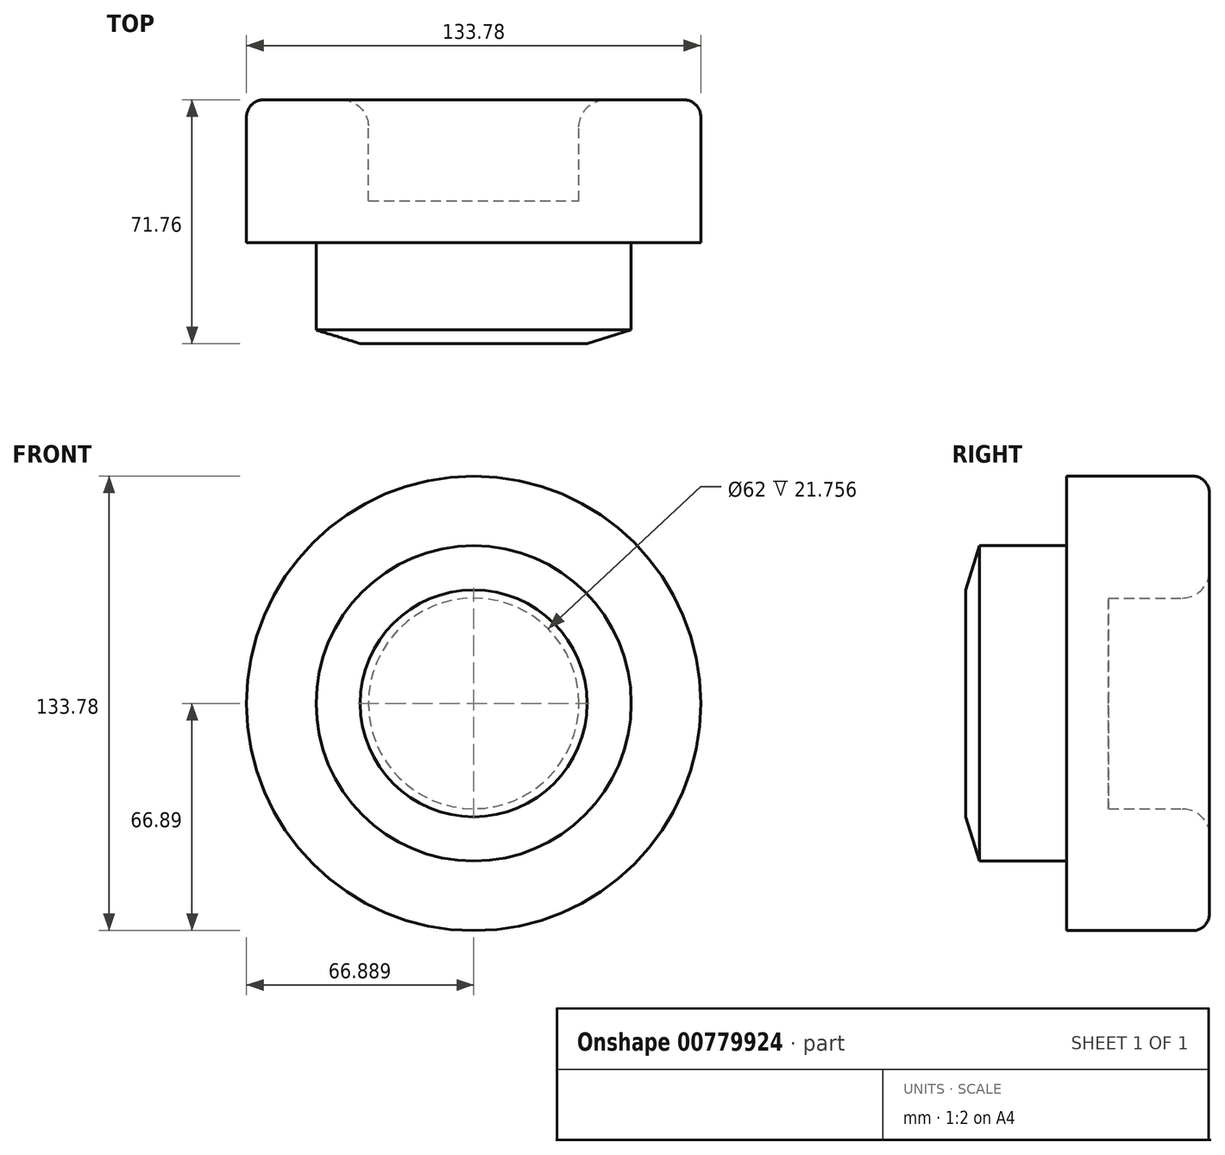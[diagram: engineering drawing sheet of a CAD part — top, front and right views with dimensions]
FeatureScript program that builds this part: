
annotation { "Feature Type Name" : "Feature", "Feature Type Description" : "" }
export const myFeature = defineFeature(function(context is Context, id is Id, definition is map)
    precondition{}
    {
        {
            var Q0;
            Q0=qCreatedBy(makeId("Top.planeOp"),FACE);
            var sketch = newSketch(context, id + "F0", { "sketchPlane" : qUnion([Q0])});
            skLineSegment(sketch, "E0.top", {"start": v(-14.36, -20) * mm, "end": v(32.04, -20) * mm});
            skLineSegment(sketch, "E0.left", {"start": v(-14.36, 22) * mm, "end": v(-14.36, -20) * mm});
            skLineSegment(sketch, "E0.right", {"start": v(32.04, 9.67) * mm, "end": v(32.04, -20) * mm});
            skLineSegment(sketch, "E1.bottom", {"start": v(16.64, 51.76) * mm, "end": v(47.53, 51.76) * mm});
            skLineSegment(sketch, "E1.top", {"start": v(32.04, 9.67) * mm, "end": v(52.53, 9.67) * mm});
            skLineSegment(sketch, "E1.right", {"start": v(52.53, 46.76) * mm, "end": v(52.53, 9.67) * mm});
            skPoint(sketch, "E2.visualSharp", {"position": v(52.53, 51.76) * mm});
            skArc(sketch, "E2.filletArc", {"start": v(52.53, 46.76) * mm, "mid": v(51.07, 50.3) * mm, "end": v(47.53, 51.76) * mm});
            skLineSegment(sketch, "E3.0", {"start": v(-14.36, 22) * mm, "end": v(16.64, 22) * mm});
            skLineSegment(sketch, "E3.1", {"start": v(16.64, 51.76) * mm, "end": v(16.64, 22) * mm});
            skSolve(sketch);
        }
        {
            var Q0;
            Q0=makeQuery(id+"F0.imprint","IMPRINT",FACE,{"disambiguationData":[TD([[makeQuery(id+"F0.imprint","IMPRINT",EDGE,{"derivedFrom":sQuery(id+"F0.wireOp",EDGE,"E0.top")}),1.0]])]});
            var Q1;
            Q1=sQuery(id+"F0.wireOp",EDGE,"E0.left");
            revolve(context, id + "F1", {"surfaceOperationType" : NewSurfaceOperationType.NEW, "entities" : qUnion([Q0]), "axis" : qUnion([Q1]), "revolveType" : RevolveType.FULL});
        }
        {
            var Q0;
            Q0=makeQuery(id+"F1.opRevolve","SWEPT_EDGE",EDGE,{"disambiguationData":[OSD([sQuery(id+"F0.wireOp",EDGE,"E1.bottom"),sQuery(id+"F0.wireOp",EDGE,"E3.1")])]});
            fillet(context, id + "F2", {"entities" : qUnion([Q0]), "radius" : 8 * mm, "tangentPropagation" : true, "allowEdgeOverflow" : false});
        }
        {
            var Q0;
            Q0=makeQuery(id+"F1.opRevolve","SWEPT_EDGE",EDGE,{"disambiguationData":[OSD([sQuery(id+"F0.wireOp",EDGE,"E0.top"),sQuery(id+"F0.wireOp",EDGE,"E0.right")])]});
            chamfer(context, id + "F3", {"entities" : qUnion([Q0]), "chamferType" : ChamferType.TWO_OFFSETS, "width1" : 4 * mm, "oppositeDirection" : false, "width2" : 13 * mm, "tangentPropagation" : true});
        }
    });
